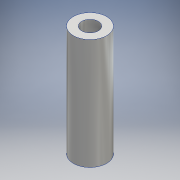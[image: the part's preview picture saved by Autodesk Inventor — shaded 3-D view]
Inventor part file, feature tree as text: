
AUTODESK INVENTOR PART (.ipt)
format: ipt  version: 2020.2 (Build 242310000, 310)  size: 116,736 bytes
history: native  units: mm
features: sketch x2, extrude x2, hole x2, other x1
ambient origin geometry x8: Origin, YZ Plane, XZ Plane, XY Plane, X Axis, Y Axis, Z Axis, Center Point
bodies: Body1 (feature_tree)
feature tree (7):
  other  "ソリッド1"
  sketch  "スケッチ1"
  extrude  "押し出し1"  Depth=6.0mm
  sketch  "スケッチ2"
  extrude  "押し出し2"  Depth=3.001mm
  hole  "穴1"  [1 undecoded]
  hole  "穴2"  [1 undecoded]
note: 2 required parameter values undecoded (feature->parameter linkage not recoverable at this tier; creation-order binding heuristic only, values carry confidence <= 0.55)
